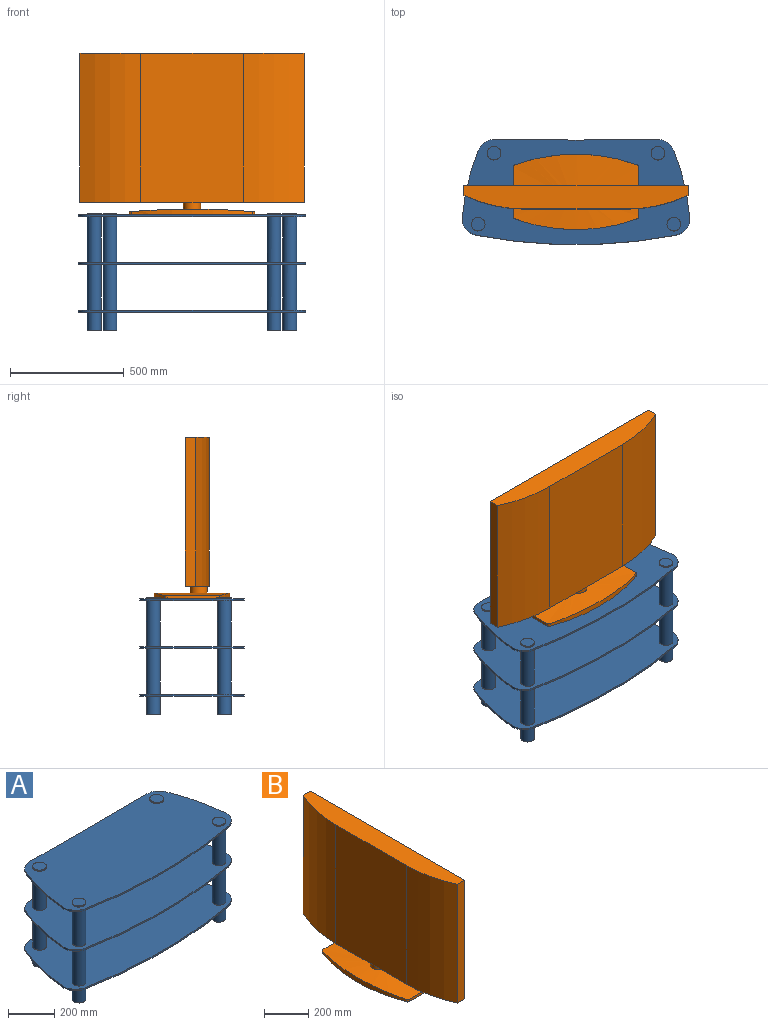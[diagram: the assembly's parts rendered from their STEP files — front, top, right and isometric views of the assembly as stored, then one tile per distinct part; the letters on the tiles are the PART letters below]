
ASSEMBLY  parts=2 mates=1
PART A: 57 faces, bbox 1000x462.2x516 mm
  f0: plane 359.53x8mm, normal (0.01,1,0), area 2876.3mm2, adj f1,f5,f6,f7
  f1: cylinder r=75mm len=69.94mm, axis (0,0,-1), area 714.5mm2, adj f0,f2,f5,f6
  f2: cylinder r=1000mm len=294.24mm, axis (0,0,-1), area 2429.4mm2, adj f1,f3,f5,f6
  f3: cylinder r=75mm len=79.87mm, axis (0,0,-1), area 879.2mm2, adj f2,f4,f5,f6
  f4: cylinder r=2348.3mm len=878.04mm, axis (0,0,-1), area 7065.9mm2, adj f3,f5,f6,f10
  f5: plane 1000x462.25mm, normal (0,0,1), area 406195.4mm2, adj f0,f1,f2,f3,f4,f7,f8,f9
  f6: plane 1000x462.25mm, normal (0,0,-1), area 406195.4mm2, adj f0,f1,f2,f3,f4,f7,f8,f9
  f7: plane 359.53x8mm, normal (-0.01,1,0), area 2876.3mm2, adj f0,f5,f6,f8
  f8: cylinder r=75mm len=69.94mm, axis (0,0,-1), area 714.5mm2, adj f5,f6,f7,f9
  f9: cylinder r=1000mm len=294.24mm, axis (0,0,-1), area 2429.4mm2, adj f5,f6,f8,f10
  f10: cylinder r=75mm len=79.87mm, axis (0,0,-1), area 879.2mm2, adj f4,f5,f6,f9
  f11: plane 60x60mm, normal (0,0,-1), area 2827.4mm2, adj f12
  f12: cylinder r=30mm len=82mm, axis (0,0,1), area 15456.6mm2, adj f6,f11
  f13: plane 60x60mm, normal (0,0,-1), area 2827.4mm2, adj f14
  f14: cylinder r=30mm len=82mm, axis (0,0,1), area 15456.6mm2, adj f6,f13
  f15: plane 60x60mm, normal (0,0,-1), area 2827.4mm2, adj f16
  f16: cylinder r=30mm len=82mm, axis (0,0,1), area 15456.6mm2, adj f6,f15
  f17: plane 60x60mm, normal (0,0,-1), area 2827.4mm2, adj f18
  f18: cylinder r=30mm len=82mm, axis (0,0,1), area 15456.6mm2, adj f6,f17
  f19: plane 359.53x8mm, normal (0.01,1,0), area 2876.3mm2, adj f20,f24,f25,f26
  f20: cylinder r=75mm len=69.94mm, axis (0,0,-1), area 714.5mm2, adj f19,f21,f24,f25
  f21: cylinder r=1000mm len=294.24mm, axis (0,0,-1), area 2429.4mm2, adj f20,f22,f24,f25
  f22: cylinder r=75mm len=79.87mm, axis (0,0,-1), area 879.2mm2, adj f21,f23,f24,f25
  f23: cylinder r=2348.3mm len=878.04mm, axis (0,0,-1), area 7065.9mm2, adj f22,f24,f25,f29
  f24: plane 1000x462.25mm, normal (0,0,1), area 406195.4mm2, adj f19,f20,f21,f22,f23,f26,f27,f28
  f25: plane 1000x462.25mm, normal (0,0,-1), area 406195.4mm2, adj f19,f20,f21,f22,f23,f26,f27,f28
  f26: plane 359.53x8mm, normal (-0.01,1,0), area 2876.3mm2, adj f19,f24,f25,f27
  f27: cylinder r=75mm len=69.94mm, axis (0,0,-1), area 714.5mm2, adj f24,f25,f26,f28
  f28: cylinder r=1000mm len=294.24mm, axis (0,0,-1), area 2429.4mm2, adj f24,f25,f27,f29
  f29: cylinder r=75mm len=79.87mm, axis (0,0,-1), area 879.2mm2, adj f23,f24,f25,f28
  f30: cylinder r=30mm len=202mm, axis (0,0,1), area 38076.1mm2, adj f5,f25
  f31: cylinder r=30mm len=202mm, axis (0,0,1), area 38076.1mm2, adj f5,f25
  f32: cylinder r=30mm len=202mm, axis (0,0,1), area 38076.1mm2, adj f5,f25
  f33: cylinder r=30mm len=202mm, axis (0,0,1), area 38076.1mm2, adj f5,f25
  f34: plane 359.53x8mm, normal (0.01,1,0), area 2876.3mm2, adj f35,f39,f40,f41
  f35: cylinder r=75mm len=69.94mm, axis (0,0,-1), area 714.5mm2, adj f34,f36,f39,f40
  f36: cylinder r=1000mm len=294.24mm, axis (0,0,-1), area 2429.4mm2, adj f35,f37,f39,f40
  f37: cylinder r=75mm len=79.87mm, axis (0,0,-1), area 879.2mm2, adj f36,f38,f39,f40
  f38: cylinder r=2348.3mm len=878.04mm, axis (0,0,-1), area 7065.9mm2, adj f37,f39,f40,f44
  f39: plane 1000x462.25mm, normal (0,0,1), area 406195.4mm2, adj f34,f35,f36,f37,f38,f41,f42,f43
  f40: plane 1000x462.25mm, normal (0,0,-1), area 406195.4mm2, adj f34,f35,f36,f37,f38,f41,f42,f43
  f41: plane 359.53x8mm, normal (-0.01,1,0), area 2876.3mm2, adj f34,f39,f40,f42
  f42: cylinder r=75mm len=69.94mm, axis (0,0,-1), area 714.5mm2, adj f39,f40,f41,f43
  f43: cylinder r=1000mm len=294.24mm, axis (0,0,-1), area 2429.4mm2, adj f39,f40,f42,f44
  f44: cylinder r=75mm len=79.87mm, axis (0,0,-1), area 879.2mm2, adj f38,f39,f40,f43
  f45: cylinder r=30mm len=202mm, axis (0,0,1), area 38076.1mm2, adj f24,f40
  f46: cylinder r=30mm len=60mm, axis (0,0,1), area 1131mm2, adj f39,f47
  f47: plane 60x60mm, normal (0,0,1), area 2827.4mm2, adj f46
  f48: cylinder r=30mm len=202mm, axis (0,0,1), area 38076.1mm2, adj f24,f40
  f49: cylinder r=30mm len=60mm, axis (0,0,1), area 1131mm2, adj f39,f50
  f50: plane 60x60mm, normal (0,0,1), area 2827.4mm2, adj f49
  f51: cylinder r=30mm len=202mm, axis (0,0,1), area 38076.1mm2, adj f24,f40
  f52: cylinder r=30mm len=60mm, axis (0,0,1), area 1131mm2, adj f39,f53
  f53: plane 60x60mm, normal (0,0,1), area 2827.4mm2, adj f52
  f54: cylinder r=30mm len=202mm, axis (0,0,1), area 38076.1mm2, adj f24,f40
  f55: cylinder r=30mm len=60mm, axis (0,0,1), area 1131mm2, adj f39,f56
  f56: plane 60x60mm, normal (0,0,1), area 2827.4mm2, adj f55
PART B: 19 faces, bbox 332.5x985x710 mm
  f0: plane 985x105mm, normal (0,0,-1), area 88520.9mm2, adj f1,f2,f3,f4,f6,f7,f14
  f1: plane 985x655mm, normal (1,0,0), area 645175mm2, adj f0,f4,f5,f7
  f2: plane 655x450mm, normal (-1,0,0), area 294750mm2, adj f0,f3,f5,f6
  f3: cylinder r=626.3mm len=655mm, axis (0,0,-1), area 181031.2mm2, adj f0,f2,f4,f5
  f4: plane 655x45mm, normal (0,-1,0), area 29475mm2, adj f0,f1,f3,f5
  f5: plane 985x105mm, normal (0,0,1), area 92938.8mm2, adj f1,f2,f3,f4,f6,f7
  f6: cylinder r=626.3mm len=655mm, axis (0,0,-1), area 181031.2mm2, adj f0,f2,f5,f7
  f7: plane 655x45mm, normal (0,1,0), area 29475mm2, adj f0,f1,f5,f6
  f8: plane 215.79x13mm, normal (0,-1,0), area 2805.3mm2, adj f9,f10,f17,f18
  f9: cylinder r=3157.04mm len=550mm, axis (1,0,0), area 160502.5mm2, adj f8,f11,f12,f13,f14,f15,f16,f17
  f10: plane 550x332.5mm, normal (0,0,-1), area 164732mm2, adj f8,f11,f12,f13,f15,f16,f17,f18
  f11: cylinder r=781.25mm len=534.21mm, axis (0,0,-1), area 11540.4mm2, adj f9,f10,f15,f17
  f12: cylinder r=781.25mm len=534.21mm, axis (0,0,-1), area 11540.4mm2, adj f9,f10,f16,f18
  f13: plane 215.79x13mm, normal (0,1,0), area 2805.3mm2, adj f9,f10,f15,f16
  f14: cylinder r=37.5mm len=75mm, axis (0,0,-1), area 7094.8mm2, adj f0,f9
  f15: cylinder r=12mm len=13.68mm, axis (0,0,-1), area 194.1mm2, adj f9,f10,f11,f13
  f16: cylinder r=12mm len=13.68mm, axis (0,0,-1), area 194.1mm2, adj f9,f10,f12,f13
  f17: cylinder r=12mm len=13.68mm, axis (0,0,-1), area 194.1mm2, adj f8,f9,f10,f11
  f18: cylinder r=12mm len=13.68mm, axis (0,0,-1), area 194.1mm2, adj f8,f9,f10,f12
PLACE A at identity fixed
PLACE B rot(axis=(0,0,1),90deg) t=(0,-46.74,428)mm
MATE fastened A.f39 <-> B.f10  axis (0,0,1) through (0,-17.99,428)mm
